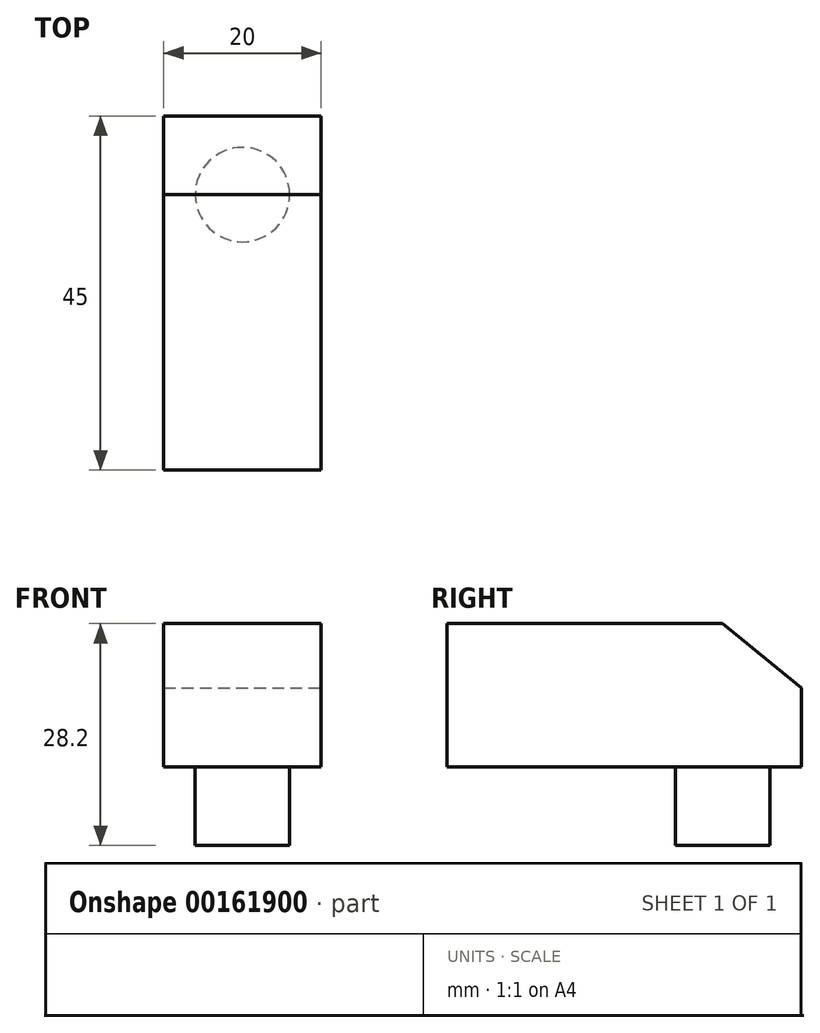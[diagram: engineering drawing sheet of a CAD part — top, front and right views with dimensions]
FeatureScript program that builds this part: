
annotation { "Feature Type Name" : "Feature", "Feature Type Description" : "" }
export const myFeature = defineFeature(function(context is Context, id is Id, definition is map)
    precondition{}
    {
        {
            var Q0;
            Q0=qCreatedBy(makeId("Right.planeOp"),FACE);
            var sketch = newSketch(context, id + "F0", { "sketchPlane" : qUnion([Q0])});
            skLineSegment(sketch, "E0.bottom", {"start": v(-22.5, -14.78) * mm, "end": v(12.5, -14.78) * mm});
            skLineSegment(sketch, "E0.top", {"start": v(-22.5, -32.98) * mm, "end": v(22.5, -32.98) * mm});
            skLineSegment(sketch, "E0.left", {"start": v(-22.5, -14.78) * mm, "end": v(-22.5, -32.98) * mm});
            skLineSegment(sketch, "E0.right", {"start": v(22.5, -22.98) * mm, "end": v(22.5, -32.98) * mm});
            skLineSegment(sketch, "E1", {"start": v(22.5, -22.98) * mm, "end": v(12.5, -14.78) * mm});
            skSolve(sketch);
        }
        {
            var Q0;
            Q0=makeQuery(id+"F0.imprint","IMPRINT",FACE,{"disambiguationData":[TD([[makeQuery(id+"F0.imprint","IMPRINT",EDGE,{"derivedFrom":sQuery(id+"F0.wireOp",EDGE,"E0.bottom")}),-1.0]])]});
            extrude(context, id + "F1", {"entities" : qUnion([Q0]), "oppositeDirection" : true, "depth" : 20 * mm});
        }
        {
            var Q0;
            Q0=makeQuery(id+"F1.opExtrude","SWEPT_FACE",FACE,{"disambiguationData":[OSD([sQuery(id+"F0.wireOp",EDGE,"E0.top")])]});
            var sketch = newSketch(context, id + "F2", { "sketchPlane" : qUnion([Q0])});
            skCircle(sketch, "E2", {"center": v(-10, -12.5) * mm, "radius": 6 * mm});
            skSolve(sketch);
        }
        {
            var Q0;
            Q0=makeQuery(id+"F2.imprint","IMPRINT",FACE,{"disambiguationData":[TD([[makeQuery(id+"F2.imprint","IMPRINT",EDGE,{"derivedFrom":sQuery(id+"F2.wireOp",EDGE,"E2")}),1.0]])]});
            extrude(context, id + "F3", {"entities" : qUnion([Q0]), "operationType" : NewBodyOperationType.ADD, "depth" : 10 * mm});
        }
    });
